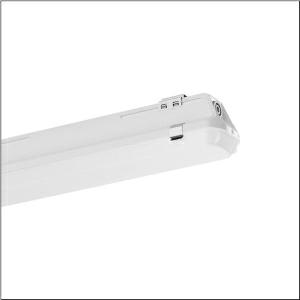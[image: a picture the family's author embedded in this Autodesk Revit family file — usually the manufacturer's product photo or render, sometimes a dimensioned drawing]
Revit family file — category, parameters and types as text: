
# Revit family: monsun_r__11_51fp109p460h_b614
name_source: partatom
category: Lighting Fixtures
units: mm (PartAtom-declared; Revit-internal decimal feet)

## family parameters
Cut with Voids When Loaded = No
Host = Face
Light Source = No
Part Type = Normal
Room Calculation Point = No
Round Connector Dimension = Use Diameter
Shared = No

## types (1)
- Monsun® 11 (1 x LED, 6100 lm, 34 W, 4000K)
    Apparent Load = 34 VA
    CIE Flux Codes = 47 77 93 94 100
    Color Rendering = 80
    Color Temperature = 4000K
    Default Elevation = 1800 mm
    Description = Monsun® 11, damp-proof luminaire, chain hanger, primary optical cover: enclosure, of PMMA, light emission: direct distribution, primary light characteristic: symmetric, installation type: suspended mounting, surface-mounted, horizontal mounting, vertical mounting, LED, rated luminous flux: 6.100lm, luminous efficacy: 179lm/W, light colour: 840, colour temperature: 4000K, control gear: ECG, with terminal, 3-pole, max. 2.5mm², mains connection: 220..240V, AC, 50/60Hz, start of lifetime: 34W, end of service life: 38W, luminaire housing, of glass-fibre reinforced polyester, uncoated, bright grey, incl. chain hanger, length: 1.590mm, width: 90mm, height: 88mm, clip for enclosure, of stainless steel (V2A), ceiling mounting element, of stainless steel (V2A), chain hanger, of stainless steel (V2A), protection rating (complete): IP66, insulation class (complete): insulation class I (protective earthing), certification: CE, ENEC, VDE, UKCA, protection symbol: D, impact resistance: IK04, permissible operating ambient temperature: -35..+40°C, standard: EN 50419, EN 60598-2-1, no direct snow, no direct sun, no direct rain, for indoor or canopied outdoor use, corresponds to IFS (International Featured Standards) requirements for safety and quality in the food industry, contact your sales advisor before using the luminaires in applications with unclear chemical exposure, large temperature fluctuations or condensation-forming humidity, LABS conformity tested according to VDMA 24364:2018-05, packaging unit: 1 piece
    Height = 89 mm
    Lamp = 1 x LED
    Lamp Light Flux = 6100 lm
    Lamp Power = 34 W
    Lamp count = 1
    Length = 1590 mm
    Luminous efficacy = 179 lm/W
    Manufacturer = Siteco
    ModVariant = No
    Model = 51FP109P460H
    Mounting Place = Ceiling
    Mounting Type = Surface mounted
    Number of Poles = 1
    OnlyDefault = Yes
    Power Factor = 1
    Product Name = Monsun® 11
    Product group = damp-proof luminaire
    ProductGroupID = 300
    Protection Class = Protection class I
    Protection Degree = IP 66
    RLX_Detail_Level = 1
    RLX_Emergency_Light_Flux = 0 lm
    RLX_Emergency_Type = 0
    RLX_Emergency_Type_DB = No
    RlxData = <blob elided: 88653 chars, md5=13d34c87>
    Socket = socket
    Standby Power = 0 W
    System Light Flux = 6100 lm
    System Power = 34 W
    Type Comments = Product without accessories
    Type Image = l_1319650.jpg
    URL = http://relux.com
    VarID = ---
    Voltage = 0 V
    Weight = 0.00 kg
    Width = 90 mm

## geometry (parser evidence)
native form markers: Blend x4, Sweep x12
no freeform markers — native parametric forms only
